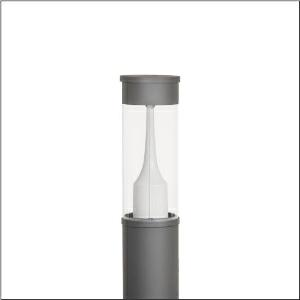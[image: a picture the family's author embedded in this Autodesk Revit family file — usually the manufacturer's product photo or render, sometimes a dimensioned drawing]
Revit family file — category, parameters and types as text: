
# Revit family: city-light_120_iq___pl1_2s_5xa5285cf14h_ce3b
name_source: partatom
category: Lighting Fixtures
units: mm (PartAtom-declared; Revit-internal decimal feet)

## family parameters
Cut with Voids When Loaded = No
Host = Face
Light Source = No
Part Type = Normal
Room Calculation Point = No
Round Connector Dimension = Use Diameter
Shared = No

## types (1)
- --- (1 x LED, 2970 lm, 23.9 W, 2200K)
    Apparent Load = 24 VA
    CIE Flux Codes = 23 62 94 96 100
    Color Rendering = 70
    Color Temperature = 2200K
    Default Elevation = 1800 mm
    Description = City-Light 120 iQ, bollard luminaire, Module 540 iQ-SR, primary light control with 3 zone facetted reflector, of plastic, silver coated, highly specular, structured, primary optical cover: cover, of PMMA, transparent, partly coated, light distribution: PL1.2s, primary light characteristic: symmetric, LED, High Power LED, rated luminous flux: 2.970lm, luminous efficacy: 124lm/W, light colour: 722, colour temperature: 2200K, control gear: ECG iQ, control: pre-setting: logarithmic dimming characteristic, Street-Remote, Auto-Match, Temp-Guard, Lumen-Switch, Night-Set, Smart-Wire, Light-Fading, Desk-Remote (wireless, voltage-free reading and setting of iQ features in the workshop via application-optimized NFC function/RFID function), optimised constant luminous flux control (CLO 2.0), with terminal, 6-pole, max. 2.5mm², mains connection: 230..240V, AC, 50/60Hz, start of lifetime: 24W, end of service life: 26W, reduction: 12W, luminaire housing, cylindrical, of extruded aluminium section, coated, Siteco® metallic grey (DB 702S), length: 1.200mm, diameter: 200mm, Module 540 iQ-SR, traffic white (RAL 9016), equipment: standard, protection rating (complete): IP54, insulation class (complete): insulation class II (safety insulation), certification: CE, ENEC, VDE, packaging unit: 1 piece

Light Distribution: PL1.2s
    Height = 500 mm
    Lamp = 1 x LED
    Lamp Light Flux = 2970 lm
    Lamp Power = 23.9 W
    Lamp count = 1
    Length = 200 mm  [stored 0.656168 ft]
    Luminous efficacy = 124 lm/W
    Manufacturer = Siteco
    ModVariant = No
    Model = 5XA5285CF14H
    Mounting Place = Floor
    Mounting Type = Freestanding
    Number of Poles = 1
    OnlyDefault = Yes
    Power Factor = 1
    Product Name = City-Light 120 iQ | PL1.2s
    Product group = bollard luminaire
    ProductGroupID = 1304
    Protection Class = Protection class II
    Protection Degree = IP 54
    RLX_Detail_Level = 1
    RLX_Emergency_Light_Flux = 0 lm
    RLX_Emergency_Type = 0
    RLX_Emergency_Type_DB = No
    RlxData = <blob elided: 30241 chars, md5=9a607ba0>
    Socket = socket
    Standby Power = 0 W
    System Light Flux = 2970 lm
    System Power = 24 W
    Type Comments = factory setting: luminous flux: 100 % | dim-lin: 254 | 499 mA
    Type Image = l_1006922.jpg
    URL = http://relux.com
    VarID = @adj_115159
    Voltage = 0 V
    Weight = 0.00 kg
    Width = 0 mm  [stored 0 ft]

note: [stored X ft] marks values corroborated as IEEE doubles in the binary element streams (Revit-internal decimal feet)

## geometry (parser evidence)
native form markers: Blend x4, Sweep x11
no freeform markers — native parametric forms only
